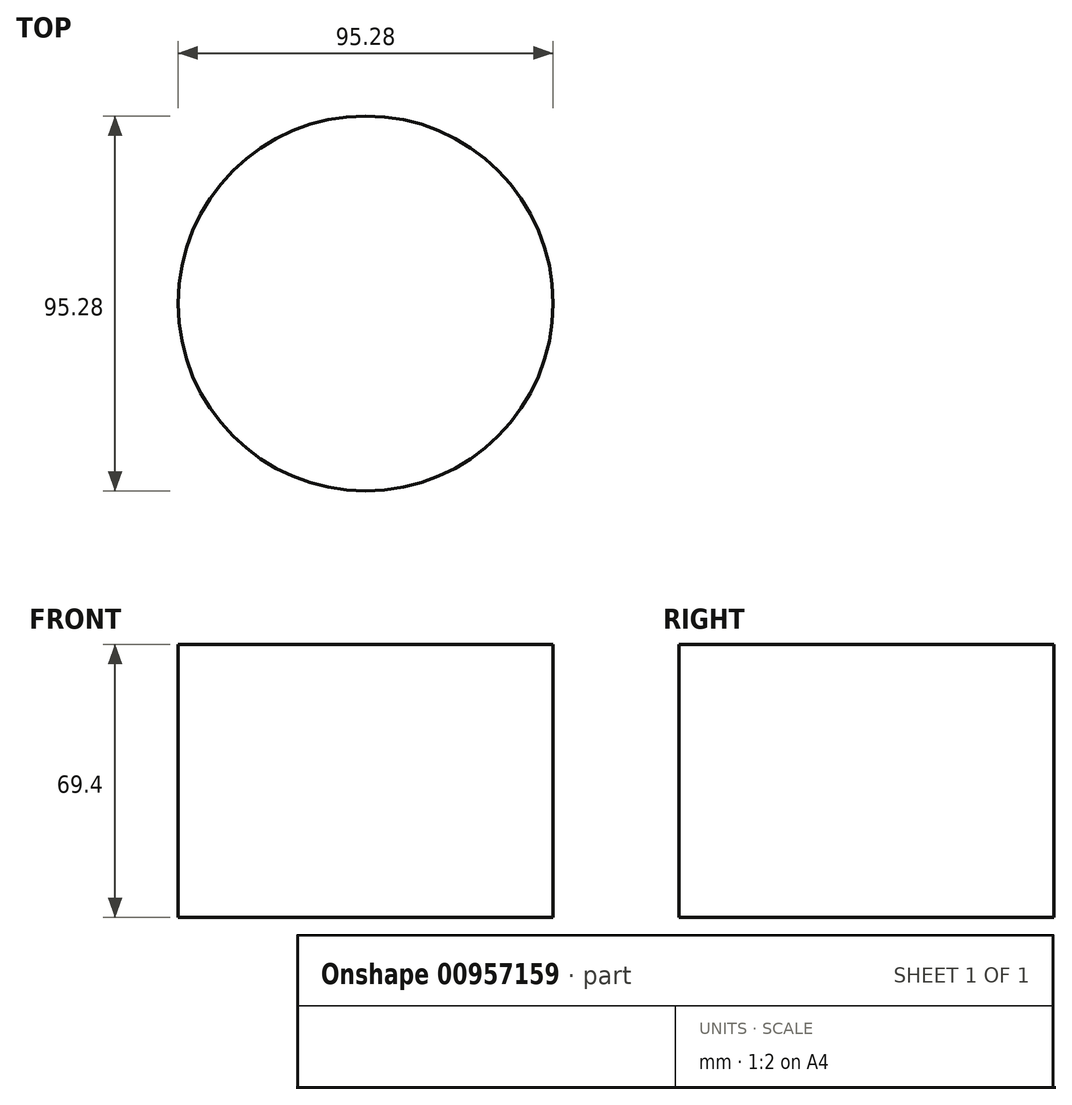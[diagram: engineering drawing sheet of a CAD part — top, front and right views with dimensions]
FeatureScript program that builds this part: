
annotation { "Feature Type Name" : "Feature", "Feature Type Description" : "" }
export const myFeature = defineFeature(function(context is Context, id is Id, definition is map)
    precondition{}
    {
        {
            var Q0;
            Q0=qCreatedBy(makeId("Top.planeOp"),FACE);
            var sketch = newSketch(context, id + "F0", { "sketchPlane" : qUnion([Q0])});
            skCircle(sketch, "E0", {"center": v(0, 0) * mm, "radius": 47.64 * mm});
            skSolve(sketch);
        }
        {
            var Q0;
            Q0=makeQuery(id+"F0.imprint","IMPRINT",FACE,{"disambiguationData":[TD([[makeQuery(id+"F0.imprint","IMPRINT",EDGE,{"derivedFrom":sQuery(id+"F0.wireOp",EDGE,"E0")}),1.0]])]});
            extrude(context, id + "F1", {"entities" : qUnion([Q0]), "depth" : 69.4 * mm, "offsetDistance" : 25 * mm});
        }
    });
